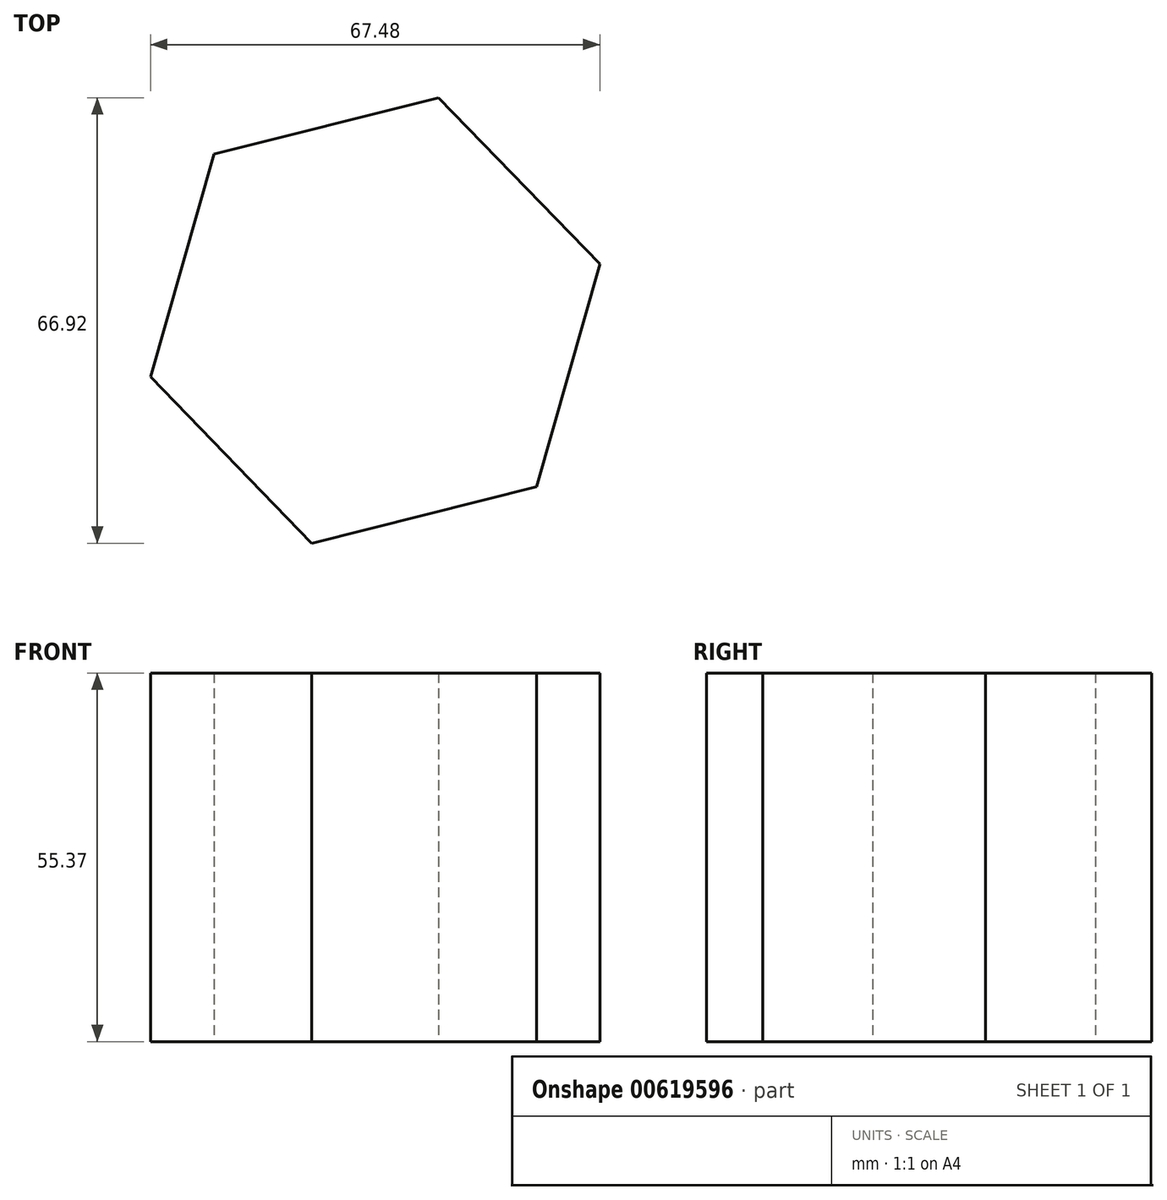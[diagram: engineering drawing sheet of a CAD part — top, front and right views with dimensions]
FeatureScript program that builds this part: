
annotation { "Feature Type Name" : "Feature", "Feature Type Description" : "" }
export const myFeature = defineFeature(function(context is Context, id is Id, definition is map)
    precondition{}
    {
        {
            var Q0;
            Q0=qCreatedBy(makeId("Top.planeOp"),FACE);
            var sketch = newSketch(context, id + "F0", { "sketchPlane" : qUnion([Q0])});
            skCircle(sketch, "E0.cCircle", {"center": v(0, 0) * mm, "radius": 30.13 * mm, "construction": true});
            skLineSegment(sketch, "E0.0", {"start": v(-24.22, 24.98) * mm, "end": v(9.52, 33.46) * mm});
            skLineSegment(sketch, "E0.1", {"start": v(9.52, 33.46) * mm, "end": v(33.74, 8.48) * mm});
            skLineSegment(sketch, "E0.2", {"start": v(33.74, 8.48) * mm, "end": v(24.22, -24.98) * mm});
            skLineSegment(sketch, "E0.3", {"start": v(24.22, -24.98) * mm, "end": v(-9.52, -33.46) * mm});
            skLineSegment(sketch, "E0.4", {"start": v(-9.52, -33.46) * mm, "end": v(-33.74, -8.48) * mm});
            skLineSegment(sketch, "E0.5", {"start": v(-33.74, -8.48) * mm, "end": v(-24.22, 24.98) * mm});
            skPoint(sketch, "E0.0.midPoint", {"position": v(-7.35, 29.22) * mm});
            skSolve(sketch);
        }
        {
            var Q0;
            Q0=makeQuery(id+"F0.imprint","IMPRINT",FACE,{"disambiguationData":[TD([[makeQuery(id+"F0.imprint","IMPRINT",EDGE,{"derivedFrom":sQuery(id+"F0.wireOp",EDGE,"E0.0")}),-1.0]])]});
            extrude(context, id + "F1", {"entities" : qUnion([Q0]), "depth" : 55.37 * mm, "offsetDistance" : 25.4 * mm});
        }
    });
